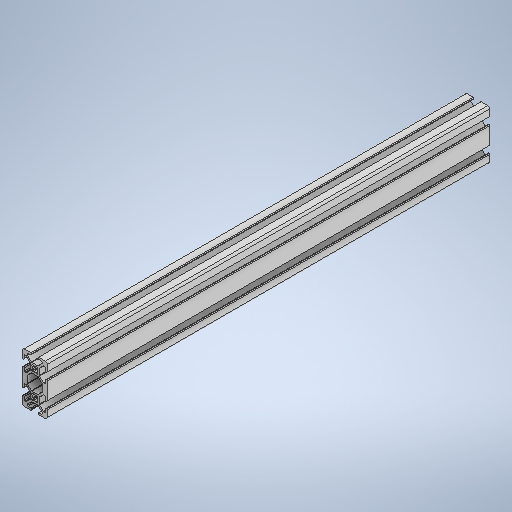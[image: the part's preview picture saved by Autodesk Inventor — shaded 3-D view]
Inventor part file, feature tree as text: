
AUTODESK INVENTOR PART (.ipt)
format: ipt  version: 2025 (Build 290162000, 162)  size: 483,328 bytes
history: native  units: in
note: dims shown in document units (in); Inventor stores cm internally (conversion verified against a paired STEP export)
features: extrude x1, sketch x1
ambient origin geometry x8: Origin, YZ Plane, XZ Plane, XY Plane, X Axis, Y Axis, Z Axis, Center Point
bodies: Solid1 (feature_tree)
feature tree (2):
  extrude  "Extrusion1"  [1 undecoded]
  sketch  "Sketch1"  dims[d0=14.0in d1=0.0in]
note: 1 required parameter value undecoded (feature->parameter linkage not recoverable at this tier; creation-order binding heuristic only, values carry confidence <= 0.55)
